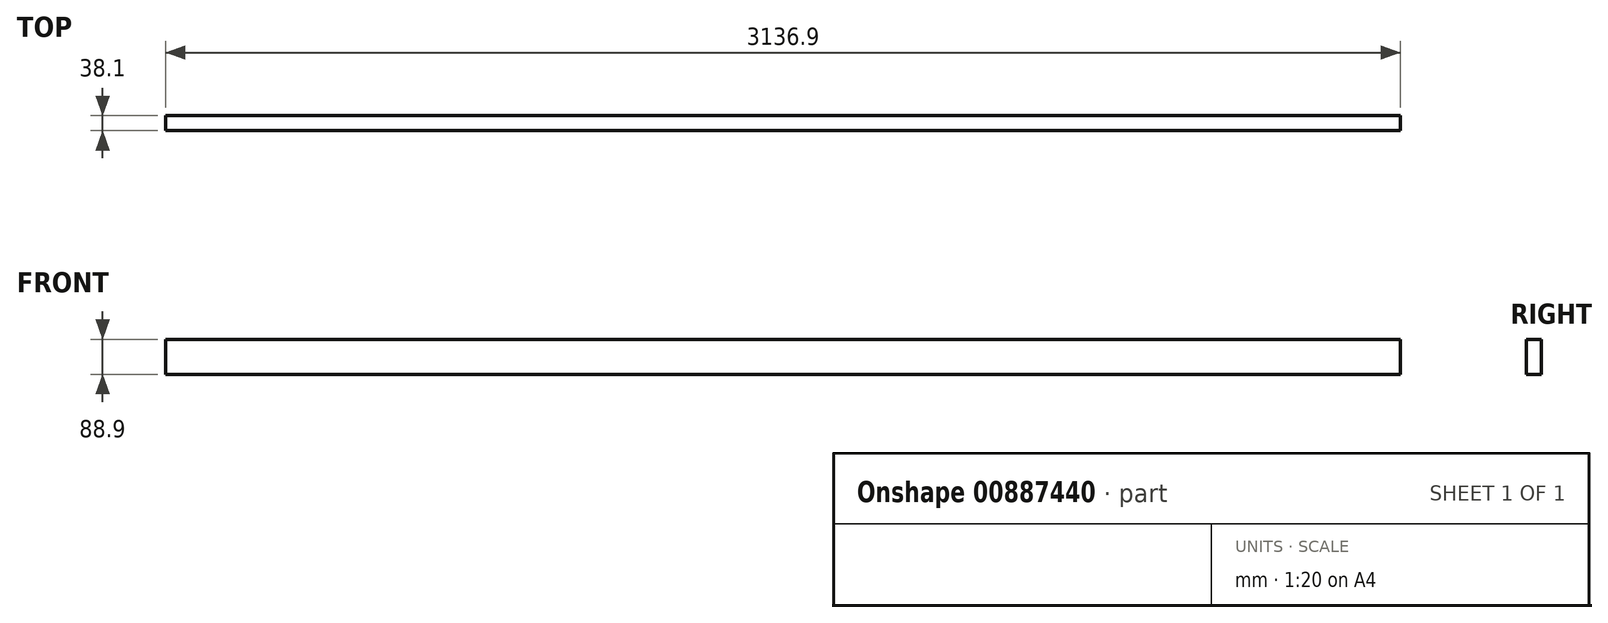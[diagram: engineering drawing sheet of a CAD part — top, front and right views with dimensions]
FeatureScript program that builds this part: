
annotation { "Feature Type Name" : "Feature", "Feature Type Description" : "" }
export const myFeature = defineFeature(function(context is Context, id is Id, definition is map)
    precondition{}
    {
        {
            var Q0;
            Q0=qCreatedBy(makeId("Top.planeOp"),FACE);
            var sketch = newSketch(context, id + "F0", { "sketchPlane" : qUnion([Q0])});
            skLineSegment(sketch, "E0.bottom", {"start": v(1568.45, 19.05) * mm, "end": v(-1568.45, 19.05) * mm});
            skLineSegment(sketch, "E0.top", {"start": v(1568.45, -19.05) * mm, "end": v(-1568.45, -19.05) * mm});
            skLineSegment(sketch, "E0.left", {"start": v(1568.45, 19.05) * mm, "end": v(1568.45, -19.05) * mm});
            skLineSegment(sketch, "E0.right", {"start": v(-1568.45, 19.05) * mm, "end": v(-1568.45, -19.05) * mm});
            skPoint(sketch, "E0.middle", {"position": v(0, 0) * mm});
            skSolve(sketch);
        }
        {
            var Q0;
            Q0=makeQuery(id+"F0.imprint","IMPRINT",FACE,{"disambiguationData":[TD([[makeQuery(id+"F0.imprint","IMPRINT",EDGE,{"derivedFrom":sQuery(id+"F0.wireOp",EDGE,"E0.bottom")}),1.0]])]});
            extrude(context, id + "F1", {"entities" : qUnion([Q0]), "depth" : 88.9 * mm, "offsetDistance" : 25.4 * mm});
        }
    });
